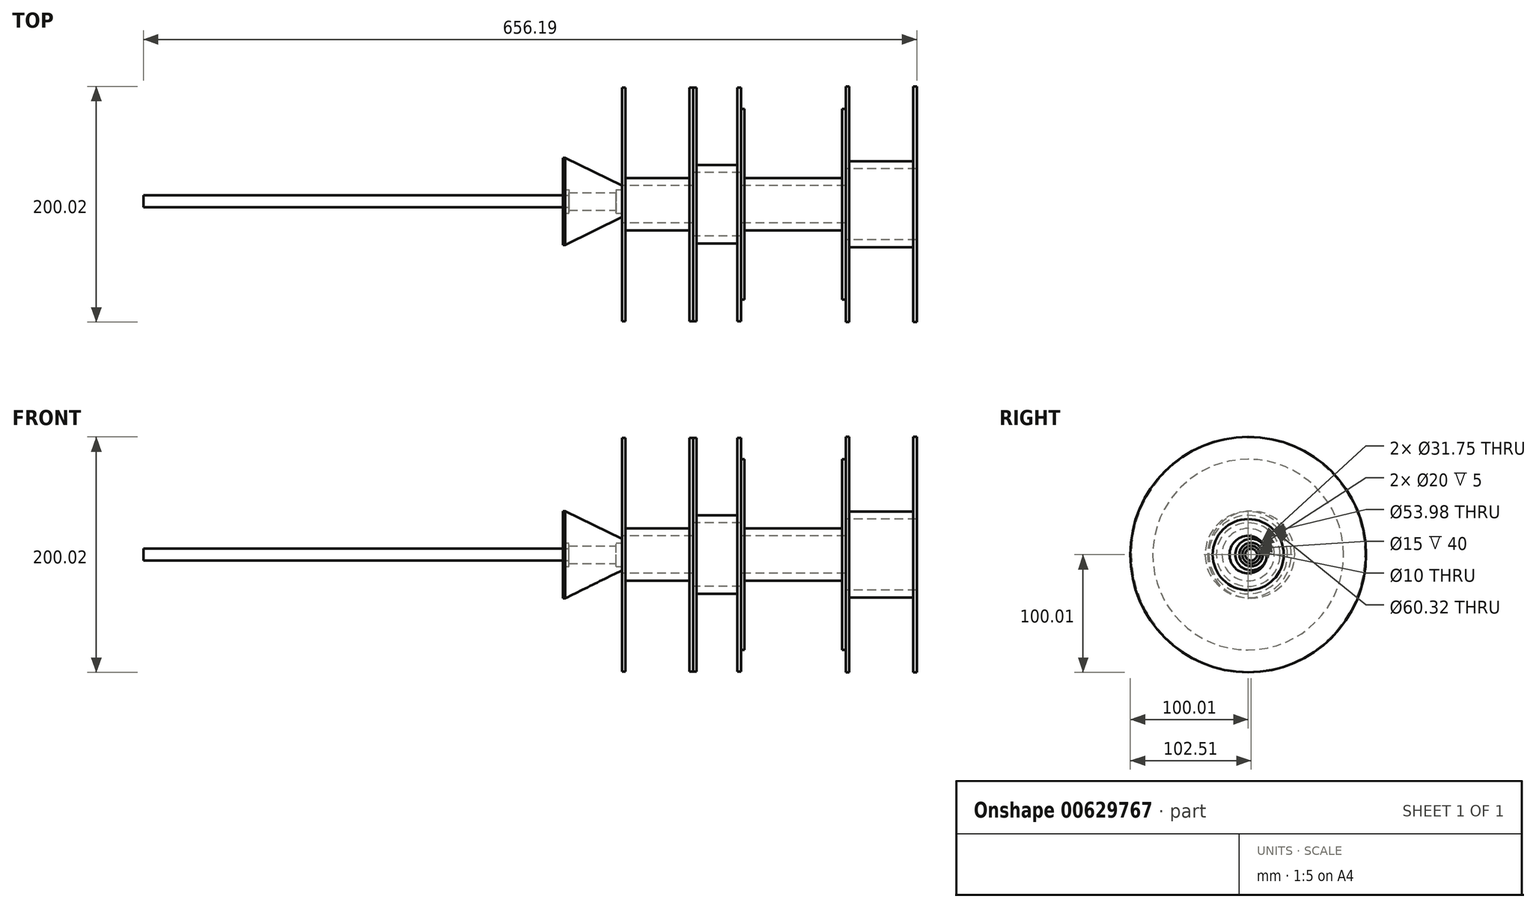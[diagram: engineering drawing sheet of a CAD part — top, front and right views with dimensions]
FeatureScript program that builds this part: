
annotation { "Feature Type Name" : "Feature", "Feature Type Description" : "" }
export const myFeature = defineFeature(function(context is Context, id is Id, definition is map)
    precondition{}
    {
        {
            var Q0;
            Q0=qCreatedBy(makeId("Front.planeOp"),FACE);
            var sketch = newSketch(context, id + "F0", { "sketchPlane" : qUnion([Q0])});
            skLineSegment(sketch, "E0", {"start": v(-30.16, 99.22) * mm, "end": v(-30.16, 15.87) * mm});
            skLineSegment(sketch, "E1", {"start": v(-30.16, 15.87) * mm, "end": v(30.16, 15.88) * mm});
            skLineSegment(sketch, "E2", {"start": v(30.16, 15.87) * mm, "end": v(30.16, 99.22) * mm});
            skLineSegment(sketch, "E3", {"start": v(30.16, 99.22) * mm, "end": v(27.16, 99.22) * mm});
            skLineSegment(sketch, "E4", {"start": v(27.16, 99.22) * mm, "end": v(27.16, 22.22) * mm});
            skLineSegment(sketch, "E5", {"start": v(27.16, 22.23) * mm, "end": v(-27.16, 22.22) * mm});
            skLineSegment(sketch, "E6", {"start": v(-27.16, 22.22) * mm, "end": v(-27.16, 99.22) * mm});
            skLineSegment(sketch, "E7", {"start": v(-27.16, 99.22) * mm, "end": v(-30.16, 99.22) * mm});
            skLineSegment(sketch, "E8", {"start": v(-30.16, 0) * mm, "end": v(30.16, 0) * mm, "construction": true});
            skSolve(sketch);
        }
        {
            var Q0;
            Q0 = qSketchRegion(id + "F0", true);
            var Q1;
            Q1=sQuery(id+"F0.wireOp",EDGE,"E8");
            revolve(context, id + "F1", {"entities" : qUnion([Q0]), "axis" : qUnion([Q1]), "revolveType" : RevolveType.FULL});
        }
        {
            var Q0;
            Q0=qCreatedBy(makeId("Front.planeOp"),FACE);
            var sketch = newSketch(context, id + "F2", { "sketchPlane" : qUnion([Q0])});
            skLineSegment(sketch, "E9", {"start": v(30.16, 99.22) * mm, "end": v(30.16, 26.99) * mm});
            skLineSegment(sketch, "E10", {"start": v(30.16, 26.99) * mm, "end": v(70.8, 26.99) * mm});
            skLineSegment(sketch, "E11", {"start": v(70.8, 26.99) * mm, "end": v(70.8, 99.22) * mm});
            skLineSegment(sketch, "E12", {"start": v(70.8, 99.22) * mm, "end": v(67.8, 99.22) * mm});
            skLineSegment(sketch, "E13", {"start": v(67.8, 99.22) * mm, "end": v(67.8, 33.34) * mm});
            skLineSegment(sketch, "E14", {"start": v(67.8, 33.34) * mm, "end": v(33.16, 33.34) * mm});
            skLineSegment(sketch, "E15", {"start": v(33.16, 33.34) * mm, "end": v(33.16, 99.22) * mm});
            skLineSegment(sketch, "E16", {"start": v(33.16, 99.22) * mm, "end": v(30.16, 99.22) * mm});
            skLineSegment(sketch, "E17", {"start": v(30.16, 0) * mm, "end": v(70.8, 0) * mm, "construction": true});
            skLineSegment(sketch, "E18.0", {"start": v(30.16, -15.88) * mm, "end": v(30.16, 15.88) * mm});
            skSolve(sketch);
        }
        {
            var Q0;
            Q0=makeQuery(id+"F2.imprint","IMPRINT",FACE,{"disambiguationData":[TD([[makeQuery(id+"F2.imprint","IMPRINT",EDGE,{"derivedFrom":sQuery(id+"F2.wireOp",EDGE,"E9")}),1.0]])]});
            var Q1;
            Q1=sQuery(id+"F2.wireOp",EDGE,"E17");
            revolve(context, id + "F3", {"entities" : qUnion([Q0]), "axis" : qUnion([Q1]), "revolveType" : RevolveType.FULL});
        }
        {
            var Q0;
            Q0=qCreatedBy(makeId("Front.planeOp"),FACE);
            var sketch = newSketch(context, id + "F4", { "sketchPlane" : qUnion([Q0])});
            skLineSegment(sketch, "E19", {"start": v(70.8, 80.96) * mm, "end": v(70.8, 15.88) * mm});
            skLineSegment(sketch, "E20", {"start": v(70.8, 15.88) * mm, "end": v(159.7, 15.88) * mm});
            skLineSegment(sketch, "E21", {"start": v(159.7, 15.88) * mm, "end": v(159.7, 80.96) * mm});
            skLineSegment(sketch, "E22", {"start": v(159.7, 80.96) * mm, "end": v(156.7, 80.96) * mm});
            skLineSegment(sketch, "E23", {"start": v(156.7, 80.96) * mm, "end": v(156.7, 22.23) * mm});
            skLineSegment(sketch, "E24", {"start": v(156.7, 22.23) * mm, "end": v(73.8, 22.23) * mm});
            skLineSegment(sketch, "E25", {"start": v(73.8, 22.23) * mm, "end": v(73.8, 80.96) * mm});
            skLineSegment(sketch, "E26", {"start": v(73.8, 80.96) * mm, "end": v(70.8, 80.96) * mm});
            skLineSegment(sketch, "E27", {"start": v(70.8, 0) * mm, "end": v(159.7, 0) * mm, "construction": true});
            skLineSegment(sketch, "E28.0", {"start": v(70.8, -26.99) * mm, "end": v(70.8, 26.99) * mm, "construction": true});
            skSolve(sketch);
        }
        {
            var Q0;
            Q0 = qSketchRegion(id + "F4", true);
            var Q1;
            Q1=sQuery(id+"F4.wireOp",EDGE,"E27");
            revolve(context, id + "F5", {"entities" : qUnion([Q0]), "axis" : qUnion([Q1]), "revolveType" : RevolveType.FULL});
        }
        {
            var Q0;
            Q0=qCreatedBy(makeId("Front.planeOp"),FACE);
            var sketch = newSketch(context, id + "F6", { "sketchPlane" : qUnion([Q0])});
            skLineSegment(sketch, "E29", {"start": v(159.7, 100.01) * mm, "end": v(159.7, 30.16) * mm});
            skLineSegment(sketch, "E30", {"start": v(159.7, 30.16) * mm, "end": v(220.03, 30.16) * mm});
            skLineSegment(sketch, "E31", {"start": v(220.03, 30.16) * mm, "end": v(220.03, 100.01) * mm});
            skLineSegment(sketch, "E32", {"start": v(220.03, 100.01) * mm, "end": v(217.03, 100.01) * mm});
            skLineSegment(sketch, "E33", {"start": v(217.03, 100.01) * mm, "end": v(217.03, 36.51) * mm});
            skLineSegment(sketch, "E34", {"start": v(217.03, 36.51) * mm, "end": v(162.7, 36.51) * mm});
            skLineSegment(sketch, "E35", {"start": v(162.7, 36.51) * mm, "end": v(162.7, 100.01) * mm});
            skLineSegment(sketch, "E36", {"start": v(162.7, 100.01) * mm, "end": v(159.7, 100.01) * mm});
            skLineSegment(sketch, "E37", {"start": v(159.7, 0) * mm, "end": v(220.03, 0) * mm, "construction": true});
            skLineSegment(sketch, "E38.0", {"start": v(159.7, -15.87) * mm, "end": v(159.7, 15.88) * mm, "construction": true});
            skSolve(sketch);
        }
        {
            var Q0;
            Q0 = qSketchRegion(id + "F6", true);
            var Q1;
            Q1=sQuery(id+"F6.wireOp",EDGE,"E37");
            revolve(context, id + "F7", {"entities" : qUnion([Q0]), "axis" : qUnion([Q1]), "revolveType" : RevolveType.FULL});
        }
        {
            var Q0;
            Q0=qCreatedBy(makeId("Top.planeOp"),FACE);
            var sketch = newSketch(context, id + "F8", { "sketchPlane" : qUnion([Q0])});
            skLineSegment(sketch, "E39", {"start": v(-30.16, 2.5) * mm, "end": v(-80.16, 2.5) * mm, "construction": true});
            skPoint(sketch, "E39.endSnap0", {"position": v(-30.16, 2.5) * mm});
            skLineSegment(sketch, "E40", {"start": v(-80.16, 39.51) * mm, "end": v(-80.16, 12.5) * mm});
            skLineSegment(sketch, "E41", {"start": v(-30.16, 15.87) * mm, "end": v(-78.16, 39.51) * mm});
            skLineSegment(sketch, "E42", {"start": v(-30.16, 12.5) * mm, "end": v(-30.16, 15.87) * mm});
            skLineSegment(sketch, "E43", {"start": v(-80.16, 12.5) * mm, "end": v(-75.16, 12.5) * mm});
            skLineSegment(sketch, "E44", {"start": v(-75.16, 12.5) * mm, "end": v(-75.16, 10) * mm});
            skLineSegment(sketch, "E45", {"start": v(-35.16, 12.5) * mm, "end": v(-35.16, 10) * mm});
            skLineSegment(sketch, "E46.trimOffspring", {"start": v(-35.16, 12.5) * mm, "end": v(-30.16, 12.5) * mm});
            skPoint(sketch, "E47.orphan", {"position": v(-80.16, 10) * mm});
            skLineSegment(sketch, "E48.trimOffspring", {"start": v(-35.16, 10) * mm, "end": v(-75.16, 10) * mm});
            skLineSegment(sketch, "E49.top", {"start": v(-80.16, 7.5) * mm, "end": v(-75.16, 7.5) * mm});
            skLineSegment(sketch, "E49.left", {"start": v(-80.16, 12.5) * mm, "end": v(-80.16, 7.5) * mm});
            skLineSegment(sketch, "E49.right", {"start": v(-75.16, 12.5) * mm, "end": v(-75.16, 7.5) * mm});
            skLineSegment(sketch, "E50", {"start": v(-80.16, 39.51) * mm, "end": v(-78.16, 39.51) * mm});
            skPoint(sketch, "E51.orphan", {"position": v(-80.16, 40.5) * mm});
            skSolve(sketch);
        }
        {
            var Q0;
            {var subQ2=sQuery(id+"F8.wireOp",EDGE,"E43");Q0=makeQuery(id+"F8.imprint","IMPRINT",FACE,{"disambiguationData":[TD([[makeQuery(id+"F8.imprint","IMPRINT",EDGE,{"derivedFrom":subQ2}),-1.0]])]});}
            var Q1;
            Q1=sQuery(id+"F8.wireOp",EDGE,"E39");
            revolve(context, id + "F9", {"entities" : qUnion([Q0]), "axis" : qUnion([Q1]), "revolveType" : RevolveType.FULL});
        }
        {
            var Q0;
            Q0=makeQuery(id+"F8.imprint","IMPRINT",FACE,{"disambiguationData":[TD([[makeQuery(id+"F8.imprint","IMPRINT",EDGE,{"derivedFrom":sQuery(id+"F8.wireOp",EDGE,"E40")}),1.0]])]});
            var Q1;
            Q1=sQuery(id+"F8.wireOp",EDGE,"E39");
            revolve(context, id + "F10", {"entities" : qUnion([Q0]), "axis" : qUnion([Q1]), "revolveType" : RevolveType.FULL});
        }
        {
            var Q0;
            Q0=makeQuery(id+"F9.opRevolve","SWEPT_FACE",FACE,{"disambiguationData":[OSD([sQuery(id+"F8.wireOp",EDGE,"E49.left")])]});
            var sketch = newSketch(context, id + "F11", { "sketchPlane" : qUnion([Q0])});
            skSolve(sketch);
        }
        {
            var Q0;
            Q0=makeQuery(id+"F11.imprint","IMPRINT",FACE,{"disambiguationData":[TD([[makeQuery(id+"F11.imprint","IMPRINT",EDGE,{"derivedFrom":makeQuery(id+"F9.opRevolve","SWEPT_EDGE",EDGE,{"disambiguationData":[OSD([sQuery(id+"F8.wireOp",EDGE,"E49.top"),sQuery(id+"F8.wireOp",EDGE,"E49.left")])]})}),-1.0]])]});
            extrude(context, id + "F12", {"entities" : qUnion([Q0]), "depth" : 356 * mm, "offsetDistance" : 25 * mm});
        }
    });
